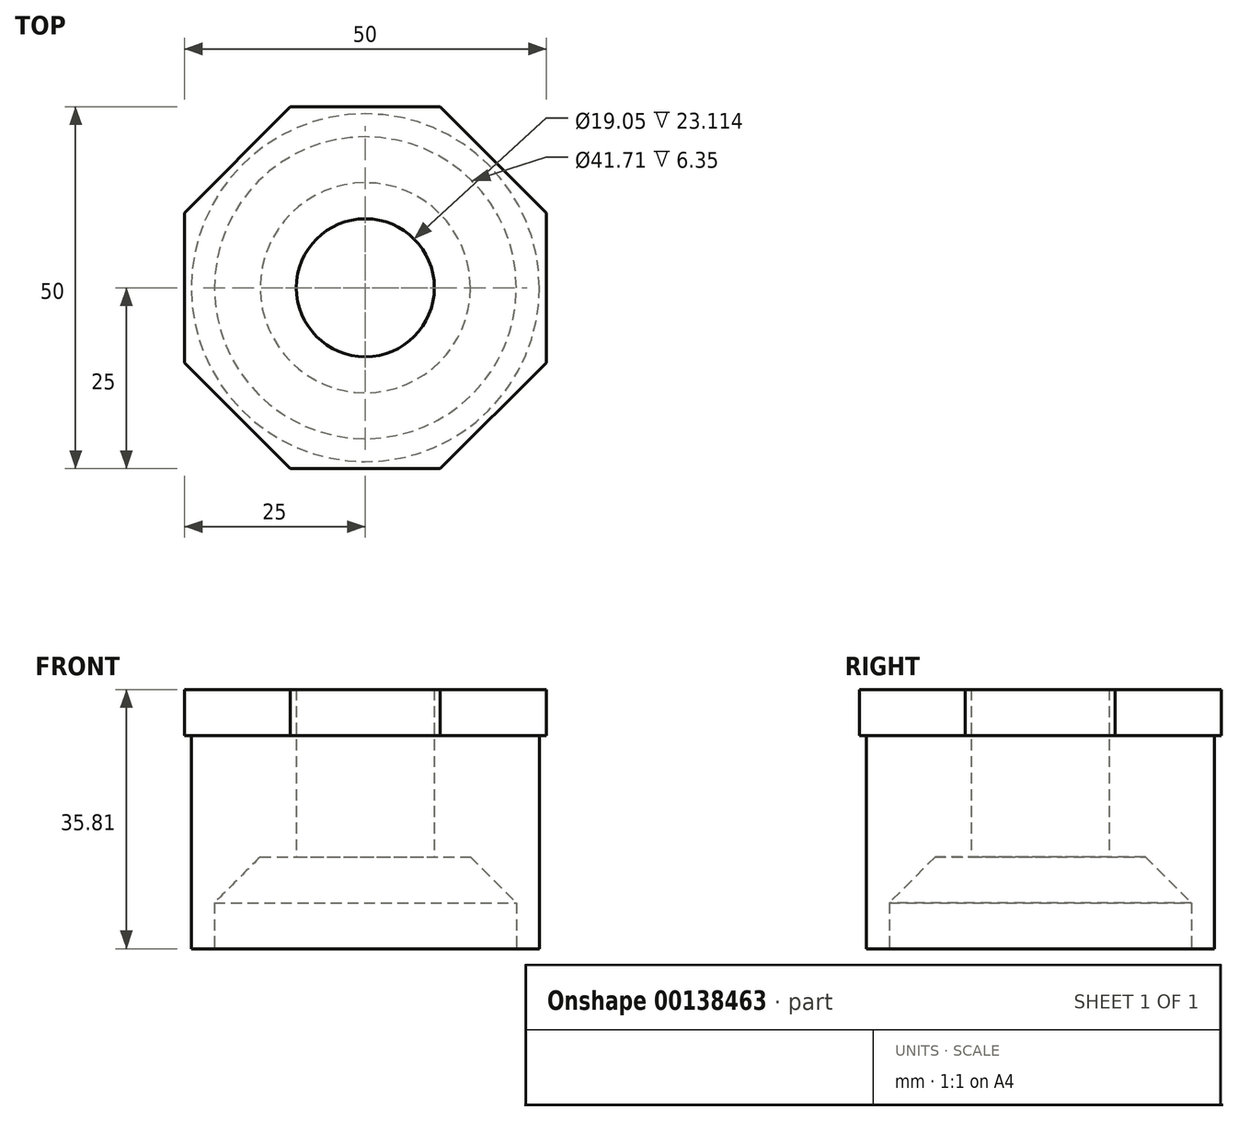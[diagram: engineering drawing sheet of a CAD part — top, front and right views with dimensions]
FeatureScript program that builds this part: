
annotation { "Feature Type Name" : "Feature", "Feature Type Description" : "" }
export const myFeature = defineFeature(function(context is Context, id is Id, definition is map)
    precondition{}
    {
        {
            var Q0;
            Q0=qCreatedBy(makeId("Top.planeOp"),FACE);
            var sketch = newSketch(context, id + "F0", { "sketchPlane" : qUnion([Q0])});
            skCircle(sketch, "E0.cCircle", {"center": v(0, 0) * mm, "radius": 25 * mm, "construction": true});
            skLineSegment(sketch, "E0.0", {"start": v(10.36, -25) * mm, "end": v(-10.36, -25) * mm});
            skLineSegment(sketch, "E0.1", {"start": v(-10.36, -25) * mm, "end": v(-25, -10.36) * mm});
            skLineSegment(sketch, "E0.2", {"start": v(-25, -10.36) * mm, "end": v(-25, 10.36) * mm});
            skLineSegment(sketch, "E0.3", {"start": v(-25, 10.36) * mm, "end": v(-10.36, 25) * mm});
            skLineSegment(sketch, "E0.4", {"start": v(-10.36, 25) * mm, "end": v(10.36, 25) * mm});
            skLineSegment(sketch, "E0.5", {"start": v(10.36, 25) * mm, "end": v(25, 10.36) * mm});
            skLineSegment(sketch, "E0.6", {"start": v(25, 10.36) * mm, "end": v(25, -10.36) * mm});
            skLineSegment(sketch, "E0.7", {"start": v(25, -10.36) * mm, "end": v(10.36, -25) * mm});
            skPoint(sketch, "E0.0.midPoint", {"position": v(0, -25) * mm});
            skCircle(sketch, "E1", {"center": v(0, 0) * mm, "radius": 9.53 * mm});
            skSolve(sketch);
        }
        {
            var Q0;
            Q0 = qSketchRegion(id + "F0", true);
            extrude(context, id + "F1", {"entities" : qUnion([Q0]), "depth" : 6.35 * mm});
        }
        {
            var Q0;
            Q0=makeQuery(id+"F1.opExtrude","CAP_FACE",FACE,{"disambiguationData":[OSD([sQuery(id+"F0.wireOp",EDGE,"E0.0"),sQuery(id+"F0.wireOp",EDGE,"E0.1"),sQuery(id+"F0.wireOp",EDGE,"E0.2"),sQuery(id+"F0.wireOp",EDGE,"E0.3"),sQuery(id+"F0.wireOp",EDGE,"E0.4"),sQuery(id+"F0.wireOp",EDGE,"E0.5"),sQuery(id+"F0.wireOp",EDGE,"E0.6"),sQuery(id+"F0.wireOp",EDGE,"E0.7"),sQuery(id+"F0.wireOp",EDGE,"E1")])],"isStart":true});
            var sketch = newSketch(context, id + "F2", { "sketchPlane" : qUnion([Q0])});
            skCircle(sketch, "E2", {"center": v(0, 0) * mm, "radius": 24.03 * mm});
            skCircle(sketch, "E3", {"center": v(0, 0) * mm, "radius": 9.53 * mm});
            skSolve(sketch);
        }
        {
            var Q0;
            Q0 = qSketchRegion(id + "F2", true);
            extrude(context, id + "F3", {"entities" : qUnion([Q0]), "operationType" : NewBodyOperationType.ADD, "depth" : 29.46 * mm});
        }
        {
            var Q0;
            Q0=makeQuery(id+"F3.opExtrude","CAP_FACE",FACE,{"disambiguationData":[OSD([sQuery(id+"F2.wireOp",EDGE,"E2"),sQuery(id+"F2.wireOp",EDGE,"E3")])],"isStart":false});
            var sketch = newSketch(context, id + "F4", { "sketchPlane" : qUnion([Q0])});
            skCircle(sketch, "E4", {"center": v(0, 0) * mm, "radius": 20.86 * mm});
            skSolve(sketch);
        }
        {
            var Q0;
            Q0 = qSketchRegion(id + "F4", true);
            extrude(context, id + "F5", {"entities" : qUnion([Q0]), "operationType" : NewBodyOperationType.REMOVE, "oppositeDirection" : true, "depth" : 12.7 * mm});
        }
        {
            var Q0;
            Q0=makeQuery(id+"F5.boolean.opBoolean","COPY",EDGE,{"derivedFrom":makeQuery(id+"F5.opExtrude","CAP_EDGE",EDGE,{"disambiguationData":[OSD([sQuery(id+"F4.wireOp",EDGE,"E4")])],"isStart":false})});
            chamfer(context, id + "F6", {"entities" : qUnion([Q0]), "width" : 6.35 * mm, "tangentPropagation" : true});
        }
    });
